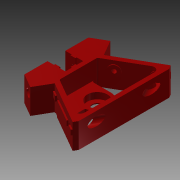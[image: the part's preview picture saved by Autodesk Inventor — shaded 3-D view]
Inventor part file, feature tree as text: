
AUTODESK INVENTOR PART (.ipt)
format: ipt  version: 2015 SP1 (Build 190203100, 203)  size: 617,984 bytes
history: native  units: mm
features: sketch x18, extrude x13, hole x5, reference x5, fillet x4, plane x4, projected_geometry x1
ambient origin geometry x8: Origin, YZ Plane, XZ Plane, XY Plane, X Axis, Y Axis, Z Axis, Center Point
bodies: Solid2 (feature_tree)
feature tree (50):
  extrude  "Extrusion13"  Depth=55.0mm
  fillet  "Fillet5"  Radius=20.0mm
  extrude  "Extrusion2"  Depth=2.0mm
  extrude  "Extrusion7"  Depth=2.0mm
  plane  "Work Plane20"
  hole  "Hole2"  [1 undecoded]
  plane  "Work Plane21"
  hole  "Hole3"  [1 undecoded]
  plane  "Work Plane18"
  hole  "Hole7"  [1 undecoded]
  plane  "Work Plane19"
  hole  "Hole8"  [1 undecoded]
  fillet  "Fillet6"  Radius=20.0mm
  extrude  "Extrusion14"  Depth=5.5mm
  extrude  "Extrusion15"  Depth=5.5mm
  extrude  "Extrusion16"  TaperAngle=60.0deg  [1 undecoded]
  extrude  "Extrusion17"  TaperAngle=60.0deg  [1 undecoded]
  extrude  "Extrusion18"  Depth=1.5mm
  extrude  "Extrusion19"  Depth=20.0mm
  extrude  "Extrusion20"  Depth=8.0mm
  extrude  "Extrusion21"  Depth=10.0mm
  fillet  "Fillet7"  Radius=10.0mm
  extrude  "Extrusion22"  Depth=10.0mm
  fillet  "Fillet8"  Radius=10.0mm
  hole  "Hole9"  [1 undecoded]
  extrude  "Extrusion23"  Depth=1.5mm
  sketch  "Sketch1"  dims[d11=20.0mm d12=55.0mm d19=20.0mm]
  sketch  "Sketch2"  dims[d23=6.0mm d24=2.0mm]
  sketch  "Sketch8"  dims[d25=6.0mm d26=2.0mm]
  sketch  "Sketch9"  dims[d27=60.0mm d28=0.0mm d63=8.0mm d64=0.0mm]
  sketch  "Sketch10"  dims[d65=4.5mm d66=6.0mm d67=10.0mm d68=32.5mm d69=90.0deg d70=30.0mm d71=20.594885mm d73=35.0mm]
  sketch  "Sketch20"  dims[d74=35.0mm]
  sketch  "Sketch21"  dims[d78=4.5mm d79=6.0mm d80=10.0mm d81=32.5mm d82=90.0deg d83=8.0mm d84=20.594885mm d110=42.5mm]
  sketch  "Sketch22"  dims[d166=20.0mm d167=0.0mm d168=20.0mm d169=20.0mm]
  sketch  "Sketch23"  dims[d171=5.5mm d172=3.0mm]
  sketch  "Sketch24"  dims[d173=5.5mm d174=3.0mm]
  sketch  "Sketch25"  dims[d176=5.0mm d177=60.0deg]
  sketch  "Sketch26"  dims[d178=120.0deg d179=60.0deg]
  sketch  "Sketch27"  dims[d181=20.0mm d184=1.5mm]
  sketch  "Sketch28"  dims[d185=5.5mm d186=20.0mm]
  reference  "Reference2"
  reference  "Reference3"
  reference  "Reference4"
  reference  "Reference5"
  reference  "Reference6"
  sketch  "Sketch29"  dims[d188=4.5mm d189=6.0mm d190=8.0mm d191=16.35mm d192=90.0deg d193=8.0mm d194=20.594885mm d195=34.865485mm]
  sketch  "Sketch30"  dims[d197=4.5mm d198=6.0mm d199=8.0mm d200=16.35mm d201=90.0deg d202=8.0mm d203=20.594885mm d204=33.0mm d205=10.0mm]
  sketch  "Sketch31"  dims[d206=5.0mm d207=33.0mm d208=10.0mm]
  sketch  "Sketch32"  dims[d209=55.0mm d210=2.0mm d211=12.0mm d212=12.0mm d213=1.0mm d214=0.0mm d215=12.0mm d216=12.0mm d217=1.0mm d218=0.0mm d219=6.25mm d220=6.25mm d221=6.25mm d222=6.25mm d223=1.0mm d224=0.0mm d225=6.25mm d226=6.25mm d227=6.25mm d228=6.25mm d229=1.0mm d230=0.0mm d231=6.25mm d232=6.25mm d233=1.0mm d234=0.0mm d235=6.25mm d236=6.25mm d237=1.0mm d238=0.0mm d239=22.5mm d240=30.0mm d241=7.0mm d242=0.0mm d243=12.0mm d244=1.0mm d245=0.0mm d246=2.0mm d247=10.0mm d248=0.0mm d249=2.0mm d250=3.0mm d251=6.0mm d252=4.0mm d253=2.0mm d254=90.0deg d255=12.0mm d256=20.594885mm d257=1.0mm d258=1.0mm d259=1.5mm d260=0.0mm]
  projected_geometry  "Projected Loop1"
note: 7 required parameter values undecoded (feature->parameter linkage not recoverable at this tier; creation-order binding heuristic only, values carry confidence <= 0.55)
